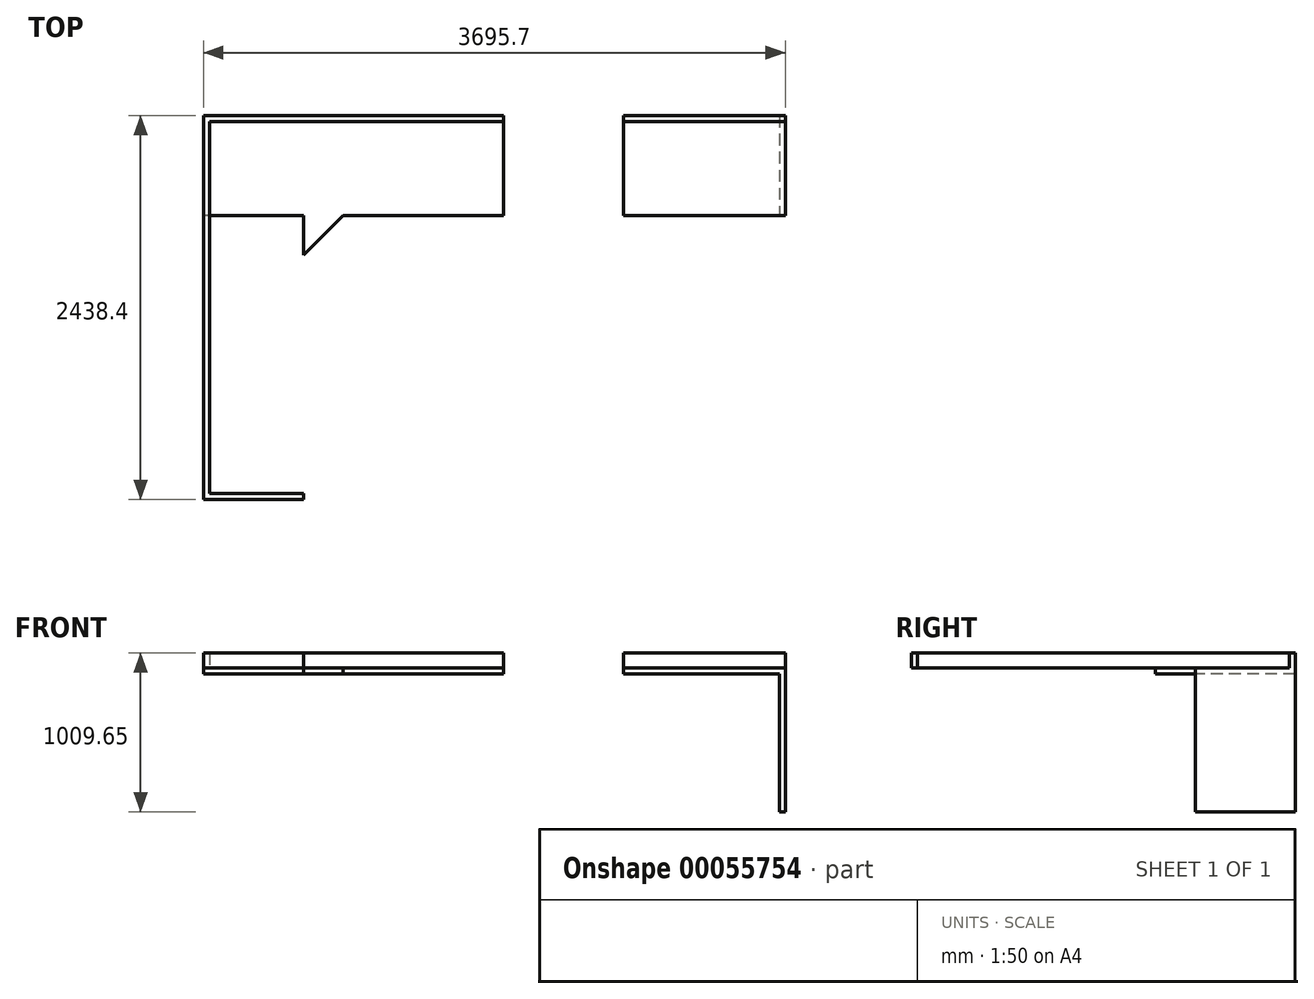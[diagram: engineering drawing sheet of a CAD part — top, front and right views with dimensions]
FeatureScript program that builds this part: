
annotation { "Feature Type Name" : "Feature", "Feature Type Description" : "" }
export const myFeature = defineFeature(function(context is Context, id is Id, definition is map)
    precondition{}
    {
        {
            var Q0;
            Q0=qCreatedBy(makeId("Top.planeOp"),FACE);
            var sketch = newSketch(context, id + "F0", { "sketchPlane" : qUnion([Q0])});
            skLineSegment(sketch, "E0.rect.bottom", {"start": v(1828.8, 317.5) * mm, "end": v(-1828.8, 317.5) * mm});
            skLineSegment(sketch, "E0.rect.top", {"start": v(1828.8, -317.5) * mm, "end": v(-1828.8, -317.5) * mm});
            skLineSegment(sketch, "E0.rect.left", {"start": v(1828.8, 317.5) * mm, "end": v(1828.8, -317.5) * mm});
            skLineSegment(sketch, "E0.rect.right", {"start": v(-1828.8, 317.5) * mm, "end": v(-1828.8, -317.5) * mm});
            skPoint(sketch, "E0.rect.middle", {"position": v(0, 0) * mm});
            skLineSegment(sketch, "E1.bottom", {"start": v(1828.8, 317.5) * mm, "end": v(1866.9, 317.5) * mm});
            skLineSegment(sketch, "E1.top", {"start": v(1828.8, -317.5) * mm, "end": v(1866.9, -317.5) * mm});
            skLineSegment(sketch, "E1.right", {"start": v(1866.9, 317.5) * mm, "end": v(1866.9, -317.5) * mm});
            skLineSegment(sketch, "E2.bottom", {"start": v(-1828.8, -317.5) * mm, "end": v(-1193.8, -317.5) * mm});
            skLineSegment(sketch, "E2.top", {"start": v(-1828.8, -2120.9) * mm, "end": v(-1193.8, -2120.9) * mm});
            skLineSegment(sketch, "E2.left", {"start": v(-1828.8, -317.5) * mm, "end": v(-1828.8, -2120.9) * mm});
            skLineSegment(sketch, "E2.right", {"start": v(-1193.8, -317.5) * mm, "end": v(-1193.8, -2120.9) * mm});
            skLineSegment(sketch, "E3", {"start": v(-1193.8, -568.95) * mm, "end": v(-942.35, -317.5) * mm});
            skSolve(sketch);
        }
        {
            var Q0;
            Q0=makeQuery(id+"F0.imprint","IMPRINT",FACE,{"disambiguationData":[TD([[makeQuery(id+"F0.imprint","IMPRINT",EDGE,{"derivedFrom":sQuery(id+"F0.wireOp",EDGE,"E0.rect.bottom")}),1.0]])]});
            var Q1;
            Q1=makeQuery(id+"F0.imprint","IMPRINT",FACE,{"disambiguationData":[TD([[makeQuery(id+"F0.imprint","IMPRINT",EDGE,{"derivedFrom":sQuery(id+"F0.wireOp",EDGE,"E2.bottom")}),-1.0]])]});
            var Q2;
            Q2=makeQuery(id+"F0.imprint","IMPRINT",FACE,{"disambiguationData":[TD([[makeQuery(id+"F0.imprint","IMPRINT",EDGE,{"derivedFrom":sQuery(id+"F0.wireOp",EDGE,"E1.bottom")}),-1.0]])]});
            var Q3;
            {var subQ3=sQuery(id+"F0.wireOp",EDGE,"E3");Q3=makeQuery(id+"F0.imprint","IMPRINT",FACE,{"disambiguationData":[TD([[makeQuery(id+"F0.imprint","IMPRINT",EDGE,{"derivedFrom":subQ3}),1.0]])]});}
            extrude(context, id + "F1", {"entities" : qUnion([Q0, Q1, Q2, Q3]), "depth" : 38.1 * mm});
        }
        {
            var Q0;
            Q0=makeQuery(id+"F0.imprint","IMPRINT",FACE,{"disambiguationData":[TD([[makeQuery(id+"F0.imprint","IMPRINT",EDGE,{"derivedFrom":sQuery(id+"F0.wireOp",EDGE,"E1.bottom")}),-1.0]])]});
            extrude(context, id + "F2", {"entities" : qUnion([Q0]), "operationType" : NewBodyOperationType.ADD, "oppositeDirection" : true, "depth" : 876.3 * mm});
        }
        {
            var Q0;
            Q0=makeQuery(id+"F1.opExtrude","CAP_FACE",FACE,{"disambiguationData":[OSD([sQuery(id+"F0.wireOp",EDGE,"E0.rect.bottom"),sQuery(id+"F0.wireOp",EDGE,"E0.rect.top"),sQuery(id+"F0.wireOp",EDGE,"E0.rect.right"),sQuery(id+"F0.wireOp",EDGE,"E1.bottom"),sQuery(id+"F0.wireOp",EDGE,"E1.top"),sQuery(id+"F0.wireOp",EDGE,"E1.right"),sQuery(id+"F0.wireOp",EDGE,"E2.top"),sQuery(id+"F0.wireOp",EDGE,"E2.left"),sQuery(id+"F0.wireOp",EDGE,"E2.right")])],"isStart":false});
            var sketch = newSketch(context, id + "F3", { "sketchPlane" : qUnion([Q0])});
            skLineSegment(sketch, "E4.bottom", {"start": v(-1828.8, -2120.9) * mm, "end": v(-1790.7, -2120.9) * mm});
            skLineSegment(sketch, "E4.top", {"start": v(-1828.8, 317.5) * mm, "end": v(-1790.7, 317.5) * mm});
            skLineSegment(sketch, "E4.left", {"start": v(-1828.8, -2120.9) * mm, "end": v(-1828.8, 317.5) * mm});
            skLineSegment(sketch, "E4.right", {"start": v(-1790.7, -2082.8) * mm, "end": v(-1790.7, 279.4) * mm});
            skLineSegment(sketch, "E5.bottom", {"start": v(-1828.8, 317.5) * mm, "end": v(1866.9, 317.5) * mm});
            skLineSegment(sketch, "E5.top", {"start": v(-1790.7, 279.4) * mm, "end": v(1866.9, 279.4) * mm});
            skLineSegment(sketch, "E5.left", {"start": v(-1828.8, 317.5) * mm, "end": v(-1828.8, 279.4) * mm});
            skLineSegment(sketch, "E5.right", {"start": v(1866.9, 317.5) * mm, "end": v(1866.9, 279.4) * mm});
            skLineSegment(sketch, "E6.bottom", {"start": v(-1790.7, -2120.9) * mm, "end": v(-1193.8, -2120.9) * mm});
            skLineSegment(sketch, "E6.top", {"start": v(-1790.7, -2082.8) * mm, "end": v(-1193.8, -2082.8) * mm});
            skLineSegment(sketch, "E6.right", {"start": v(-1193.8, -2120.9) * mm, "end": v(-1193.8, -2082.8) * mm});
            skSolve(sketch);
        }
        {
            var Q0;
            Q0=qSketchRegion(id+"F3",true);
            extrude(context, id + "F4", {"entities" : qUnion([Q0]), "operationType" : NewBodyOperationType.ADD, "depth" : 95.25 * mm});
        }
        {
            var Q0;
            Q0=makeQuery(id+"F1.opExtrude","CAP_FACE",FACE,{"disambiguationData":[OSD([sQuery(id+"F0.wireOp",EDGE,"E0.rect.bottom"),sQuery(id+"F0.wireOp",EDGE,"E0.rect.top"),sQuery(id+"F0.wireOp",EDGE,"E0.rect.right"),sQuery(id+"F0.wireOp",EDGE,"E1.bottom"),sQuery(id+"F0.wireOp",EDGE,"E1.top"),sQuery(id+"F0.wireOp",EDGE,"E1.right"),sQuery(id+"F0.wireOp",EDGE,"E2.top"),sQuery(id+"F0.wireOp",EDGE,"E2.left"),sQuery(id+"F0.wireOp",EDGE,"E2.right"),sQuery(id+"F0.wireOp",EDGE,"E3")])],"isStart":false});
            var sketch = newSketch(context, id + "F5", { "sketchPlane" : qUnion([Q0])});
            skLineSegment(sketch, "E7.bottom", {"start": v(838.2, -317.5) * mm, "end": v(76.2, -317.5) * mm});
            skLineSegment(sketch, "E7.top", {"start": v(838.2, 489.68) * mm, "end": v(76.2, 489.68) * mm});
            skLineSegment(sketch, "E7.left", {"start": v(838.2, -317.5) * mm, "end": v(838.2, 489.68) * mm});
            skLineSegment(sketch, "E7.right", {"start": v(76.2, -317.5) * mm, "end": v(76.2, 489.68) * mm});
            skSolve(sketch);
        }
        {
            var Q0;
            Q0 = qSketchRegion(id + "F5", true);
            extrude(context, id + "F6", {"entities" : qUnion([Q0]), "operationType" : NewBodyOperationType.REMOVE, "oppositeDirection" : true, "depth" : 203.2 * mm, "hasSecondDirection" : true, "secondDirectionOppositeDirection" : false, "secondDirectionDepth" : 203.2 * mm});
        }
        {
            var Q0;
            {var subQ0=sQuery(id+"F0.wireOp",EDGE,"E1.top");var subQ1=sQuery(id+"F0.wireOp",EDGE,"E2.right");var subQ2=sQuery(id+"F0.wireOp",EDGE,"E3");var subQ3=sQuery(id+"F0.wireOp",EDGE,"E0.rect.top");Q0=makeQuery(id+"F6.boolean.opBoolean","SPLIT",FACE,{"disambiguationData":[TD([makeQuery(id+"F1.opExtrude","SWEPT_FACE",FACE,{"disambiguationData":[OSD([subQ1])]})])],"derivedFrom":makeQuery(id+"F1.opExtrude","CAP_FACE",FACE,{"disambiguationData":[OSD([sQuery(id+"F0.wireOp",EDGE,"E0.rect.bottom"),subQ3,sQuery(id+"F0.wireOp",EDGE,"E0.rect.right"),sQuery(id+"F0.wireOp",EDGE,"E1.bottom"),subQ0,sQuery(id+"F0.wireOp",EDGE,"E1.right"),sQuery(id+"F0.wireOp",EDGE,"E2.top"),sQuery(id+"F0.wireOp",EDGE,"E2.left"),subQ1,subQ2])],"isStart":false})});}
            var sketch = newSketch(context, id + "F7", { "sketchPlane" : qUnion([Q0])});
            skLineSegment(sketch, "E8.rect.bottom", {"start": v(-1346.2, -647.7) * mm, "end": v(-1600.2, -647.7) * mm});
            skLineSegment(sketch, "E8.rect.top", {"start": v(-1346.2, -1460.5) * mm, "end": v(-1600.2, -1460.5) * mm});
            skLineSegment(sketch, "E8.rect.left", {"start": v(-1244.6, -749.3) * mm, "end": v(-1244.6, -1358.9) * mm});
            skLineSegment(sketch, "E8.rect.right", {"start": v(-1701.8, -749.3) * mm, "end": v(-1701.8, -1358.9) * mm});
            skPoint(sketch, "E8.rect.middle", {"position": v(-1473.2, -1054.1) * mm});
            skPoint(sketch, "E9.visualSharp", {"position": v(-1701.8, -1460.5) * mm});
            skArc(sketch, "E9.filletArc", {"start": v(-1701.8, -1358.9) * mm, "mid": v(-1672.04, -1430.74) * mm, "end": v(-1600.2, -1460.5) * mm});
            skPoint(sketch, "E10.visualSharp", {"position": v(-1244.6, -1460.5) * mm});
            skArc(sketch, "E10.filletArc", {"start": v(-1346.2, -1460.5) * mm, "mid": v(-1274.36, -1430.74) * mm, "end": v(-1244.6, -1358.9) * mm});
            skPoint(sketch, "E11.visualSharp", {"position": v(-1701.8, -647.7) * mm});
            skArc(sketch, "E11.filletArc", {"start": v(-1600.2, -647.7) * mm, "mid": v(-1672.04, -677.46) * mm, "end": v(-1701.8, -749.3) * mm});
            skPoint(sketch, "E12.visualSharp", {"position": v(-1244.6, -647.7) * mm});
            skArc(sketch, "E12.filletArc", {"start": v(-1244.6, -749.3) * mm, "mid": v(-1274.36, -677.46) * mm, "end": v(-1346.2, -647.7) * mm});
            skLineSegment(sketch, "E13", {"start": v(-1473.2, -1054.1) * mm, "end": v(-1739.9, -1054.1) * mm, "construction": true});
            skPoint(sketch, "E13.endSnap0", {"position": v(-1701.8, -1054.1) * mm});
            skCircle(sketch, "E14", {"center": v(-1739.9, -1054.1) * mm, "radius": 12.7 * mm});
            skSolve(sketch);
        }
        {
            var Q0;
            Q0 = qSketchRegion(id + "F7", true);
            extrude(context, id + "F8", {"entities" : qUnion([Q0]), "operationType" : NewBodyOperationType.REMOVE, "oppositeDirection" : true, "depth" : 127 * mm});
        }
    });
